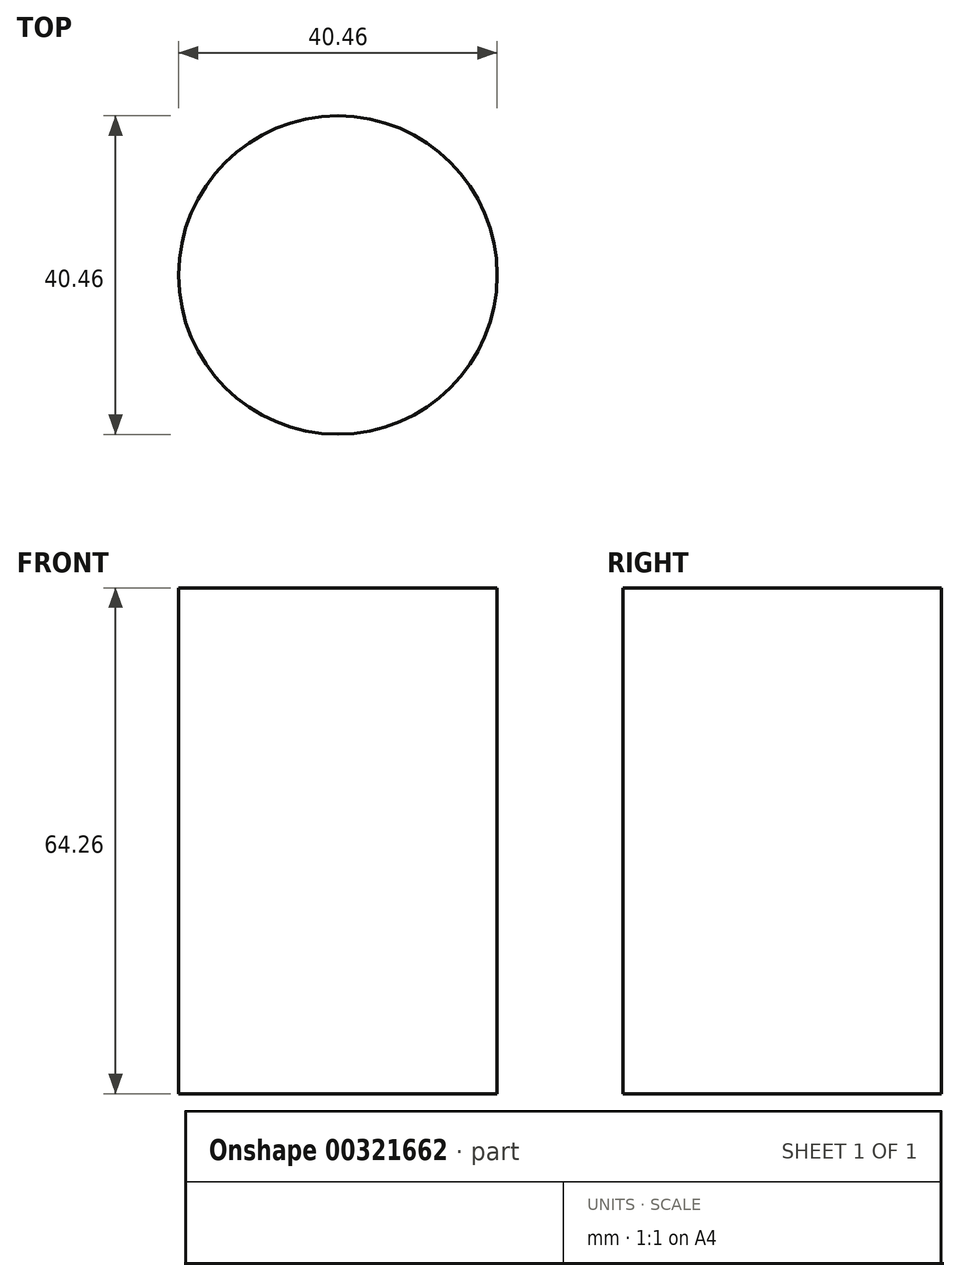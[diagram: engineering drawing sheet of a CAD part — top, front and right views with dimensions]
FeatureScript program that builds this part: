
annotation { "Feature Type Name" : "Feature", "Feature Type Description" : "" }
export const myFeature = defineFeature(function(context is Context, id is Id, definition is map)
    precondition{}
    {
        {
            var Q0;
            Q0=qCreatedBy(makeId("Top.planeOp"),FACE);
            var sketch = newSketch(context, id + "F0", { "sketchPlane" : qUnion([Q0])});
            skCircle(sketch, "E0", {"center": v(-28.78, 15.03) * mm, "radius": 20.23 * mm});
            skCircle(sketch, "E1", {"center": v(-28.78, 15.03) * mm, "radius": 32.14 * mm});
            skSolve(sketch);
        }
        {
            var Q0;
            Q0=makeQuery(id+"F0.imprint","IMPRINT",FACE,{"disambiguationData":[TD([[makeQuery(id+"F0.imprint","IMPRINT",EDGE,{"derivedFrom":sQuery(id+"F0.wireOp",EDGE,"E0")}),1.0]])]});
            extrude(context, id + "F1", {"entities" : qUnion([Q0]), "oppositeDirection" : true, "depth" : 64.26 * mm});
        }
    });
